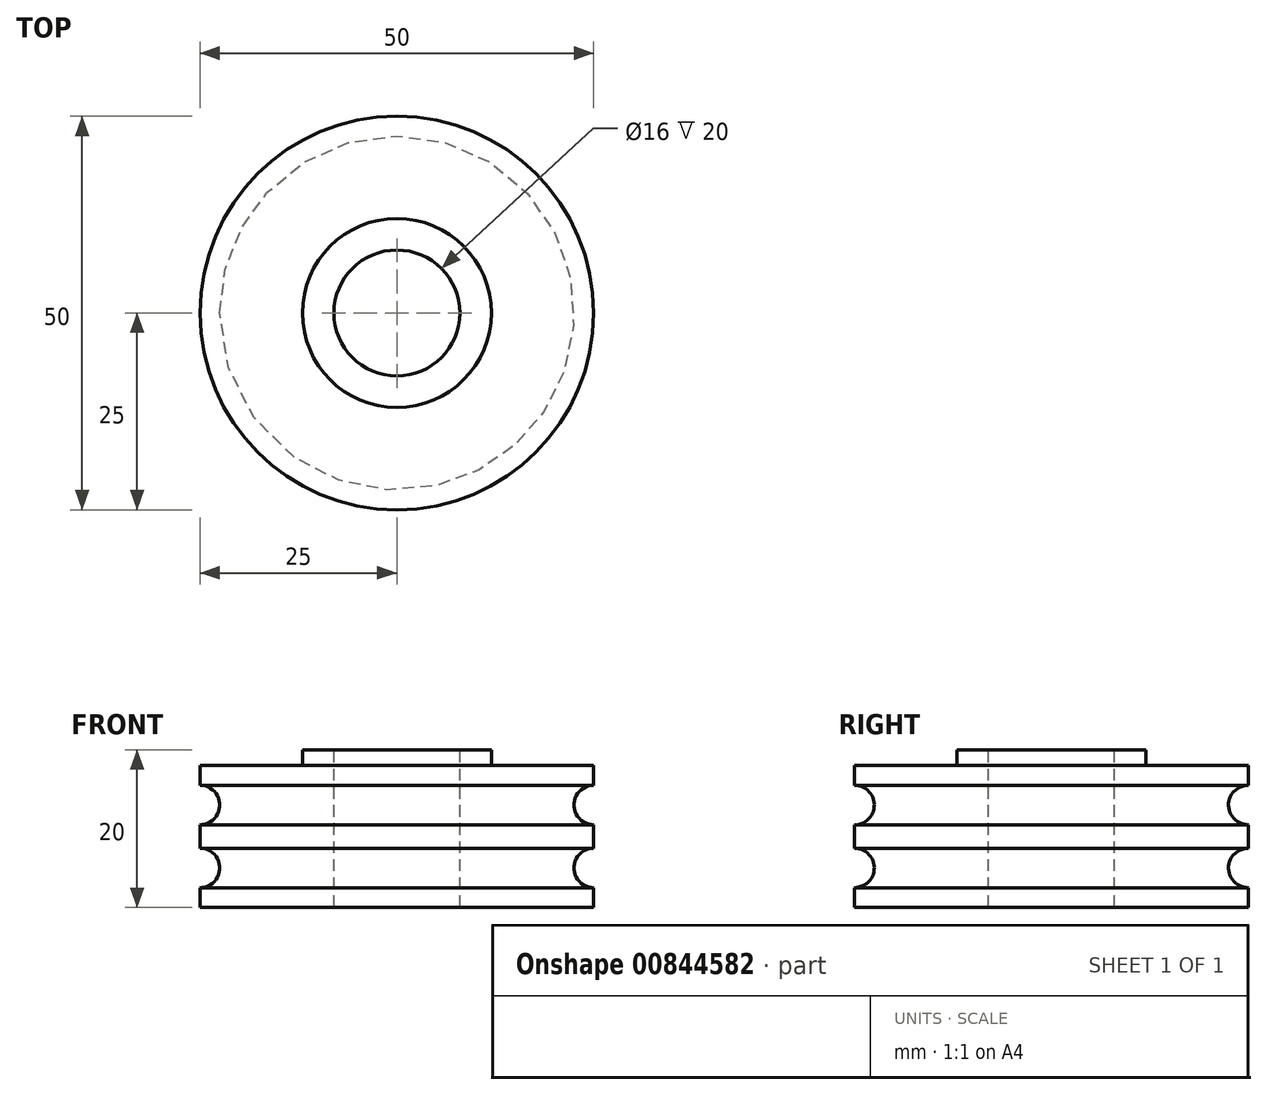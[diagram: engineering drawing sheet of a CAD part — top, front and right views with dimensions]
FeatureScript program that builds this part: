
annotation { "Feature Type Name" : "Feature", "Feature Type Description" : "" }
export const myFeature = defineFeature(function(context is Context, id is Id, definition is map)
    precondition{}
    {
        {
            var Q0;
            Q0=qCreatedBy(makeId("Top.planeOp"),FACE);
            var sketch = newSketch(context, id + "F0", { "sketchPlane" : qUnion([Q0])});
            skCircle(sketch, "E0", {"center": v(0, 0) * mm, "radius": 25 * mm});
            skSolve(sketch);
        }
        {
            var Q0;
            Q0 = qSketchRegion(id + "F0", true);
            extrude(context, id + "F1", {"entities" : qUnion([Q0]), "depth" : 18 * mm, "offsetDistance" : 25 * mm});
        }
        {
            var Q0;
            Q0=makeQuery(id+"F1.opExtrude","CAP_FACE",FACE,{"disambiguationData":[OSD([sQuery(id+"F0.wireOp",EDGE,"E0")])],"isStart":false});
            var sketch = newSketch(context, id + "F2", { "sketchPlane" : qUnion([Q0])});
            skCircle(sketch, "E1", {"center": v(0, 0) * mm, "radius": 12 * mm});
            skSolve(sketch);
        }
        {
            var Q0;
            Q0 = qSketchRegion(id + "F2", true);
            extrude(context, id + "F3", {"entities" : qUnion([Q0]), "operationType" : NewBodyOperationType.ADD, "depth" : 2 * mm, "offsetDistance" : 25 * mm});
        }
        {
            var Q0;
            Q0=makeQuery(id+"F3.opExtrude","CAP_FACE",FACE,{"disambiguationData":[OSD([sQuery(id+"F2.wireOp",EDGE,"E1")])],"isStart":false});
            var sketch = newSketch(context, id + "F4", { "sketchPlane" : qUnion([Q0])});
            skCircle(sketch, "E2", {"center": v(0, 0) * mm, "radius": 8 * mm});
            skSolve(sketch);
        }
        {
            var Q0;
            Q0=makeQuery(id+"F4.imprint","IMPRINT",FACE,{"disambiguationData":[TD([[makeQuery(id+"F4.imprint","IMPRINT",EDGE,{"derivedFrom":sQuery(id+"F4.wireOp",EDGE,"E2")}),1.0]])]});
            extrude(context, id + "F5", {"entities" : qUnion([Q0]), "operationType" : NewBodyOperationType.REMOVE, "oppositeDirection" : true, "depth" : 25 * mm, "offsetDistance" : 25 * mm});
        }
        {
            var Q0;
            Q0=qCreatedBy(makeId("Front.planeOp"),FACE);
            var sketch = newSketch(context, id + "F6", { "sketchPlane" : qUnion([Q0])});
            skCircle(sketch, "E3", {"center": v(25, 5) * mm, "radius": 2.5 * mm});
            skCircle(sketch, "E4", {"center": v(25, 13) * mm, "radius": 2.5 * mm});
            skSolve(sketch);
        }
        {
            var Q0;
            Q0=qCreatedBy(makeId("Right.planeOp"),FACE);
            var sketch = newSketch(context, id + "F7", { "sketchPlane" : qUnion([Q0])});
            skLineSegment(sketch, "E5", {"start": v(0, 34.59) * mm, "end": v(0, -19.07) * mm, "construction": true});
            skSolve(sketch);
        }
        {
            var Q0;
            Q0=makeQuery(id+"F6.imprint","IMPRINT",FACE,{"disambiguationData":[TD([[makeQuery(id+"F6.imprint","IMPRINT",EDGE,{"derivedFrom":sQuery(id+"F6.wireOp",EDGE,"E4")}),1.0]])]});
            var Q1;
            Q1=makeQuery(id+"F6.imprint","IMPRINT",FACE,{"disambiguationData":[TD([[makeQuery(id+"F6.imprint","IMPRINT",EDGE,{"derivedFrom":sQuery(id+"F6.wireOp",EDGE,"E3")}),1.0]])]});
            var Q2;
            Q2=sQuery(id+"F7.wireOp",EDGE,"E5");
            revolve(context, id + "F8", {"operationType" : NewBodyOperationType.REMOVE, "surfaceOperationType" : NewSurfaceOperationType.NEW, "entities" : qUnion([Q0, Q1]), "axis" : qUnion([Q2]), "revolveType" : RevolveType.FULL, "oppositeDirection" : true});
        }
    });
